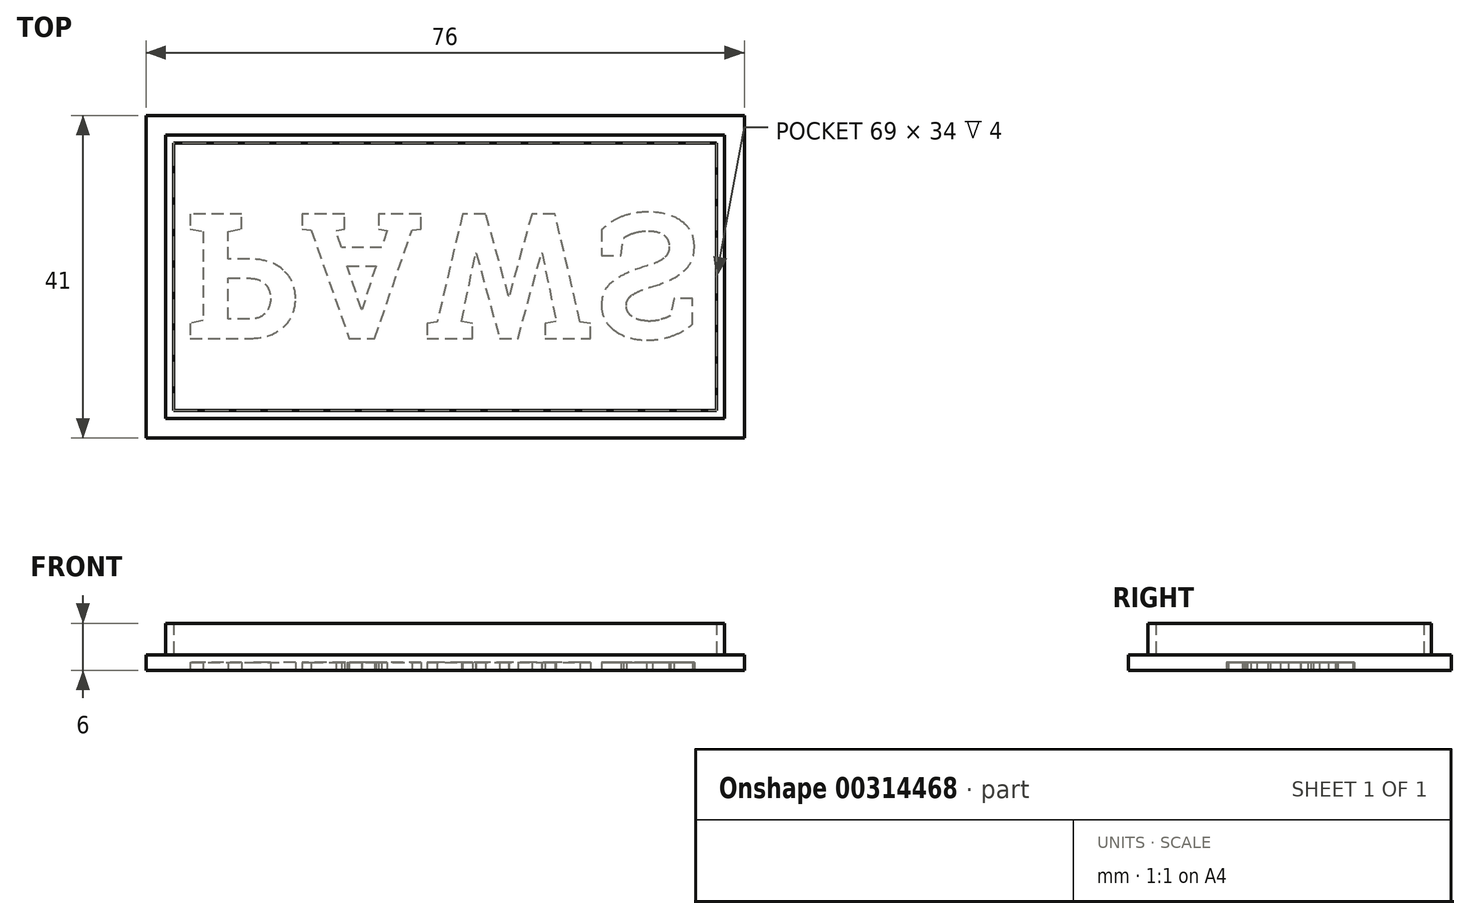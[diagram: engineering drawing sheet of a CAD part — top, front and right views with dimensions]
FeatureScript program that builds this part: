
annotation { "Feature Type Name" : "Feature", "Feature Type Description" : "" }
export const myFeature = defineFeature(function(context is Context, id is Id, definition is map)
    precondition{}
    {
        {
            var Q0;
            Q0=qCreatedBy(makeId("Top.planeOp"),FACE);
            var sketch = newSketch(context, id + "F0", { "sketchPlane" : qUnion([Q0])});
            skLineSegment(sketch, "E0.bottom", {"start": v(0, 0) * mm, "end": v(76, 0) * mm});
            skLineSegment(sketch, "E0.top", {"start": v(0, -41) * mm, "end": v(76, -41) * mm});
            skLineSegment(sketch, "E0.left", {"start": v(0, 0) * mm, "end": v(0, -41) * mm});
            skLineSegment(sketch, "E0.right", {"start": v(76, 0) * mm, "end": v(76, -41) * mm});
            skSolve(sketch);
        }
        {
            var Q0;
            Q0 = qSketchRegion(id + "F0", true);
            extrude(context, id + "F1", {"entities" : qUnion([Q0]), "depth" : 2 * mm});
        }
        {
            var Q0;
            Q0=makeQuery(id+"F1.opExtrude","CAP_FACE",FACE,{"disambiguationData":[OSD([sQuery(id+"F0.wireOp",EDGE,"E0.bottom"),sQuery(id+"F0.wireOp",EDGE,"E0.top"),sQuery(id+"F0.wireOp",EDGE,"E0.left"),sQuery(id+"F0.wireOp",EDGE,"E0.right")])],"isStart":false});
            var sketch = newSketch(context, id + "F2", { "sketchPlane" : qUnion([Q0])});
            skLineSegment(sketch, "E1.bottom", {"start": v(2.5, -2.5) * mm, "end": v(73.5, -2.5) * mm});
            skLineSegment(sketch, "E1.top", {"start": v(2.5, -38.5) * mm, "end": v(73.5, -38.5) * mm});
            skLineSegment(sketch, "E1.left", {"start": v(2.5, -2.5) * mm, "end": v(2.5, -38.5) * mm});
            skLineSegment(sketch, "E1.right", {"start": v(73.5, -2.5) * mm, "end": v(73.5, -38.5) * mm});
            skLineSegment(sketch, "E2.bottom", {"start": v(3.5, -3.5) * mm, "end": v(72.5, -3.5) * mm});
            skLineSegment(sketch, "E2.top", {"start": v(3.5, -37.5) * mm, "end": v(72.5, -37.5) * mm});
            skLineSegment(sketch, "E2.left", {"start": v(3.5, -3.5) * mm, "end": v(3.5, -37.5) * mm});
            skLineSegment(sketch, "E2.right", {"start": v(72.5, -3.5) * mm, "end": v(72.5, -37.5) * mm});
            skSolve(sketch);
        }
        {
            var Q0;
            Q0 = qSketchRegion(id + "F2", true);
            extrude(context, id + "F3", {"entities" : qUnion([Q0]), "operationType" : NewBodyOperationType.ADD, "depth" : 4 * mm});
        }
        {
            var Q0;
            Q0=makeQuery(id+"F1.opExtrude","CAP_FACE",FACE,{"disambiguationData":[OSD([sQuery(id+"F0.wireOp",EDGE,"E0.bottom"),sQuery(id+"F0.wireOp",EDGE,"E0.top"),sQuery(id+"F0.wireOp",EDGE,"E0.left"),sQuery(id+"F0.wireOp",EDGE,"E0.right")])],"isStart":true});
            var sketch = newSketch(context, id + "F4", { "sketchPlane" : qUnion([Q0])});
            skText(sketch, "E3", { "text": "PAWS", "fontName": "RobotoSlab-Bold.ttf"});
            const initialGuessF4  = {"E3": [0.005, 0.0125, 1, 0, 0.01602]};
            skSetInitialGuess(sketch, initialGuessF4);
            skSolve(sketch);
        }
        {
            var Q0;
            Q0 = qSketchRegion(id + "F4", true);
            extrude(context, id + "F5", {"entities" : qUnion([Q0]), "operationType" : NewBodyOperationType.REMOVE, "oppositeDirection" : true, "depth" : 1 * mm});
        }
    });
